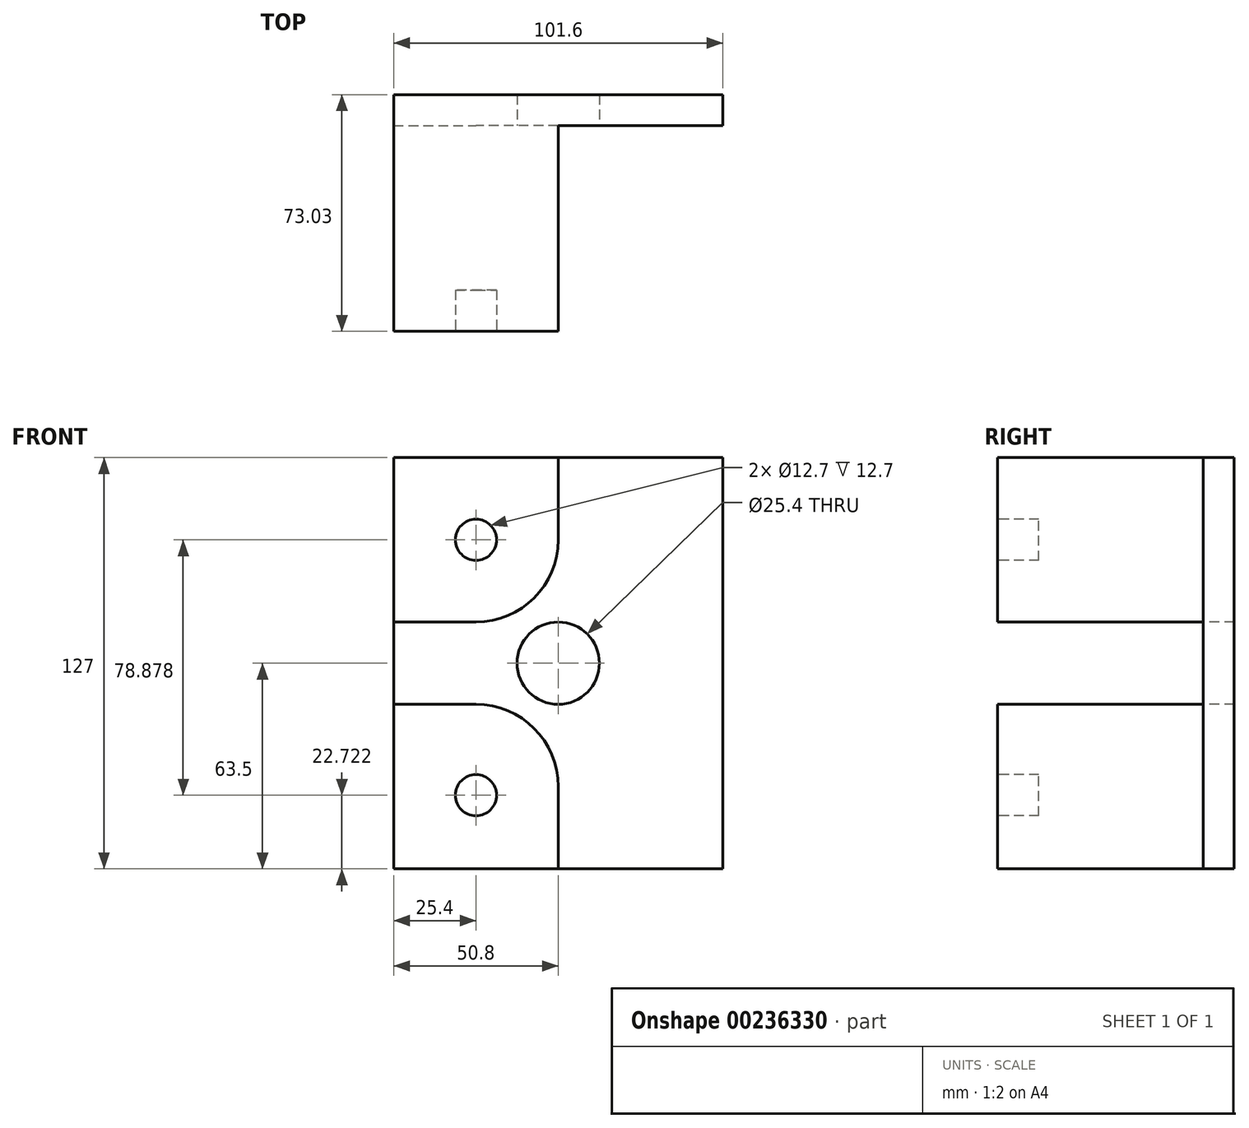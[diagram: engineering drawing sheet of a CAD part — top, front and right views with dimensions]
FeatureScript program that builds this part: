
annotation { "Feature Type Name" : "Feature", "Feature Type Description" : "" }
export const myFeature = defineFeature(function(context is Context, id is Id, definition is map)
    precondition{}
    {
        {
            var Q0;
            Q0=qCreatedBy(makeId("Front.planeOp"),FACE);
            var sketch = newSketch(context, id + "F0", { "sketchPlane" : qUnion([Q0])});
            skLineSegment(sketch, "E0.bottom", {"start": v(-50.8, 63.5) * mm, "end": v(50.8, 63.5) * mm});
            skLineSegment(sketch, "E0.top", {"start": v(-50.8, -63.5) * mm, "end": v(50.8, -63.5) * mm});
            skLineSegment(sketch, "E0.left", {"start": v(-50.8, 63.5) * mm, "end": v(-50.8, -63.5) * mm});
            skLineSegment(sketch, "E0.right", {"start": v(50.8, 63.5) * mm, "end": v(50.8, -63.5) * mm});
            skPoint(sketch, "E0.middle", {"position": v(0, 0) * mm});
            skSolve(sketch);
        }
        {
            var Q0;
            Q0=makeQuery(id+"F0.imprint","IMPRINT",FACE,{"disambiguationData":[TD([[makeQuery(id+"F0.imprint","IMPRINT",EDGE,{"derivedFrom":sQuery(id+"F0.wireOp",EDGE,"E0.bottom")}),-1.0]])]});
            extrude(context, id + "F1", {"entities" : qUnion([Q0]), "depth" : 9.52 * mm});
        }
        {
            var Q0;
            Q0=makeQuery(id+"F1.opExtrude","CAP_FACE",FACE,{"disambiguationData":[OSD([sQuery(id+"F0.wireOp",EDGE,"E0.bottom"),sQuery(id+"F0.wireOp",EDGE,"E0.top"),sQuery(id+"F0.wireOp",EDGE,"E0.left"),sQuery(id+"F0.wireOp",EDGE,"E0.right")])],"isStart":false});
            var sketch = newSketch(context, id + "F2", { "sketchPlane" : qUnion([Q0])});
            skCircle(sketch, "E1", {"center": v(0, 0) * mm, "radius": 12.7 * mm});
            skSolve(sketch);
        }
        {
            var Q0;
            Q0=makeQuery(id+"F2.imprint","IMPRINT",FACE,{"disambiguationData":[TD([[makeQuery(id+"F2.imprint","IMPRINT",EDGE,{"derivedFrom":sQuery(id+"F2.wireOp",EDGE,"E1")}),1.0]])]});
            extrude(context, id + "F3", {"entities" : qUnion([Q0]), "operationType" : NewBodyOperationType.REMOVE, "oppositeDirection" : true, "depth" : 63.5 * mm});
        }
        {
            var Q0;
            Q0=makeQuery(id+"F1.opExtrude","CAP_FACE",FACE,{"disambiguationData":[OSD([sQuery(id+"F0.wireOp",EDGE,"E0.bottom"),sQuery(id+"F0.wireOp",EDGE,"E0.top"),sQuery(id+"F0.wireOp",EDGE,"E0.left"),sQuery(id+"F0.wireOp",EDGE,"E0.right")])],"isStart":false});
            var sketch = newSketch(context, id + "F4", { "sketchPlane" : qUnion([Q0])});
            skLineSegment(sketch, "E2.bottom", {"start": v(-50.8, -63.5) * mm, "end": v(0, -63.5) * mm});
            skLineSegment(sketch, "E2.top", {"start": v(-50.8, -12.7) * mm, "end": v(0, -12.7) * mm});
            skLineSegment(sketch, "E2.left", {"start": v(-50.8, -63.5) * mm, "end": v(-50.8, -12.7) * mm});
            skLineSegment(sketch, "E2.right", {"start": v(0, -63.5) * mm, "end": v(0, -12.7) * mm});
            skSolve(sketch);
        }
        {
            var Q0;
            Q0=makeQuery(id+"F4.imprint","IMPRINT",FACE,{"disambiguationData":[TD([[makeQuery(id+"F4.imprint","IMPRINT",EDGE,{"derivedFrom":sQuery(id+"F4.wireOp",EDGE,"E2.bottom")}),1.0]])]});
            extrude(context, id + "F5", {"entities" : qUnion([Q0]), "operationType" : NewBodyOperationType.ADD, "depth" : 63.5 * mm});
        }
        {
            var Q0;
            Q0=makeQuery(id+"F1.opExtrude","CAP_FACE",FACE,{"disambiguationData":[OSD([sQuery(id+"F0.wireOp",EDGE,"E0.bottom"),sQuery(id+"F0.wireOp",EDGE,"E0.top"),sQuery(id+"F0.wireOp",EDGE,"E0.left"),sQuery(id+"F0.wireOp",EDGE,"E0.right")])],"isStart":false});
            var sketch = newSketch(context, id + "F6", { "sketchPlane" : qUnion([Q0])});
            skLineSegment(sketch, "E3.bottom", {"start": v(-50.8, 63.5) * mm, "end": v(0, 63.5) * mm});
            skLineSegment(sketch, "E3.top", {"start": v(-50.8, 12.7) * mm, "end": v(0, 12.7) * mm});
            skLineSegment(sketch, "E3.left", {"start": v(-50.8, 63.5) * mm, "end": v(-50.8, 12.7) * mm});
            skLineSegment(sketch, "E3.right", {"start": v(0, 63.5) * mm, "end": v(0, 12.7) * mm});
            skSolve(sketch);
        }
        {
            var Q0;
            Q0=makeQuery(id+"F6.imprint","IMPRINT",FACE,{"disambiguationData":[TD([[makeQuery(id+"F6.imprint","IMPRINT",EDGE,{"derivedFrom":sQuery(id+"F6.wireOp",EDGE,"E3.bottom")}),-1.0]])]});
            extrude(context, id + "F7", {"entities" : qUnion([Q0]), "operationType" : NewBodyOperationType.ADD, "depth" : 63.5 * mm});
        }
        {
            var Q0;
            Q0=makeQuery(id+"F5.opExtrude","SWEPT_EDGE",EDGE,{"disambiguationData":[OSD([sQuery(id+"F2.wireOp",EDGE,"E1"),sQuery(id+"F4.wireOp",EDGE,"E2.top"),sQuery(id+"F4.wireOp",EDGE,"E2.right")])]});
            fillet(context, id + "F8", {"entities" : qUnion([Q0]), "radius" : 25.4 * mm, "tangentPropagation" : true, "allowEdgeOverflow" : false});
        }
        {
            var Q0;
            Q0=makeQuery(id+"F7.opExtrude","SWEPT_EDGE",EDGE,{"disambiguationData":[OSD([sQuery(id+"F2.wireOp",EDGE,"E1"),sQuery(id+"F6.wireOp",EDGE,"E3.top"),sQuery(id+"F6.wireOp",EDGE,"E3.right")])]});
            fillet(context, id + "F9", {"entities" : qUnion([Q0]), "radius" : 25.4 * mm, "tangentPropagation" : true, "allowEdgeOverflow" : false});
        }
        {
            var Q0;
            Q0=makeQuery(id+"F5.opExtrude","CAP_FACE",FACE,{"disambiguationData":[OSD([sQuery(id+"F4.wireOp",EDGE,"E2.bottom"),sQuery(id+"F4.wireOp",EDGE,"E2.top"),sQuery(id+"F4.wireOp",EDGE,"E2.left"),sQuery(id+"F4.wireOp",EDGE,"E2.right")])],"isStart":false});
            var sketch = newSketch(context, id + "F10", { "sketchPlane" : qUnion([Q0])});
            skCircle(sketch, "E4", {"center": v(-25.4, -40.78) * mm, "radius": 6.35 * mm});
            skSolve(sketch);
        }
        {
            var Q0;
            Q0 = qSketchRegion(id + "F10", true);
            extrude(context, id + "F11", {"entities" : qUnion([Q0]), "operationType" : NewBodyOperationType.REMOVE, "oppositeDirection" : true, "depth" : 12.7 * mm});
        }
        {
            var Q0;
            Q0=makeQuery(id+"F7.opExtrude","CAP_FACE",FACE,{"disambiguationData":[OSD([sQuery(id+"F6.wireOp",EDGE,"E3.bottom"),sQuery(id+"F6.wireOp",EDGE,"E3.top"),sQuery(id+"F6.wireOp",EDGE,"E3.left"),sQuery(id+"F6.wireOp",EDGE,"E3.right")])],"isStart":false});
            var sketch = newSketch(context, id + "F12", { "sketchPlane" : qUnion([Q0])});
            skCircle(sketch, "E5", {"center": v(-25.4, 38.1) * mm, "radius": 6.35 * mm});
            skSolve(sketch);
        }
        {
            var Q0;
            Q0=makeQuery(id+"F12.imprint","IMPRINT",FACE,{"disambiguationData":[TD([[makeQuery(id+"F12.imprint","IMPRINT",EDGE,{"derivedFrom":sQuery(id+"F12.wireOp",EDGE,"E5")}),1.0]])]});
            extrude(context, id + "F13", {"entities" : qUnion([Q0]), "operationType" : NewBodyOperationType.REMOVE, "oppositeDirection" : true, "depth" : 12.7 * mm});
        }
    });
